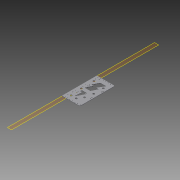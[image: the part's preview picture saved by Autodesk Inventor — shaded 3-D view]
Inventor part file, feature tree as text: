
AUTODESK INVENTOR PART (.ipt)
format: ipt  version: 2015 (Build 190159000, 159)  size: 203,264 bytes
history: native  units: in
note: dims shown in document units (in); Inventor stores cm internally (conversion verified against a paired STEP export)
features: sketch x8, extrude x7, plane x1, hole x1, pattern_linear x1, fillet x1, projected_geometry x1
ambient origin geometry x8: Origin, YZ Plane, XZ Plane, XY Plane, X Axis, Y Axis, Z Axis, Center Point
bodies: Solid1 (feature_tree)
feature tree (20):
  plane  "Work Plane1"
  extrude  "Extrusion1"  Depth=7.0in
  extrude  "Extrusion2"  Depth=0.09in TaperAngle=0.0deg
  hole  "Hole1"  [1 undecoded]
  pattern_linear  "Rectangular Pattern1"  Count1=5 Spacing1=0.5in
  extrude  "Extrusion3"  Depth=0.09in TaperAngle=0.0deg
  sketch  "Sketch6"  dims[d20=0.09in d21=0.0in d22=0.09in d23=0.0in]
  extrude  "Extrusion4"  Depth=0.25in TaperAngle=0.0deg
  fillet  "Fillet2"  Radius=0.4in
  extrude  "Extrusion5"  Depth=0.4in
  extrude  "Extrusion6"  Depth=0.09in
  extrude  "Extrusion7"  Depth=0.09in
  sketch  "Sketch1"  dims[d0=7.0in d1=3.5in]
  sketch  "Sketch2"  dims[d2=0.09in d3=0.0in d5=0.09in d6=0.0in]
  projected_geometry  "Projected Loop1"
  sketch  "Sketch3"  dims[d7=0.15in d8=0.15in]
  sketch  "Sketch4"  dims[d9=0.129in d10=0.75in d11=0.375in d12=0.25in d13=0.5635in d14=0.09in d15=0.8108in d16=1.9685in d18=0.5in]
  sketch  "Sketch7"  dims[d24=0.25in d25=1.0in d26=0.0in d27=0.4in]
  sketch  "Sketch8"  dims[d28=0.4in d29=0.4in]
  sketch  "Sketch9"  dims[d30=0.4in d31=0.4in d32=0.4in d33=0.4in d34=1.0in d35=0.0in d36=0.09in d37=0.0in]
note: 1 required parameter value undecoded (feature->parameter linkage not recoverable at this tier; creation-order binding heuristic only, values carry confidence <= 0.55)
